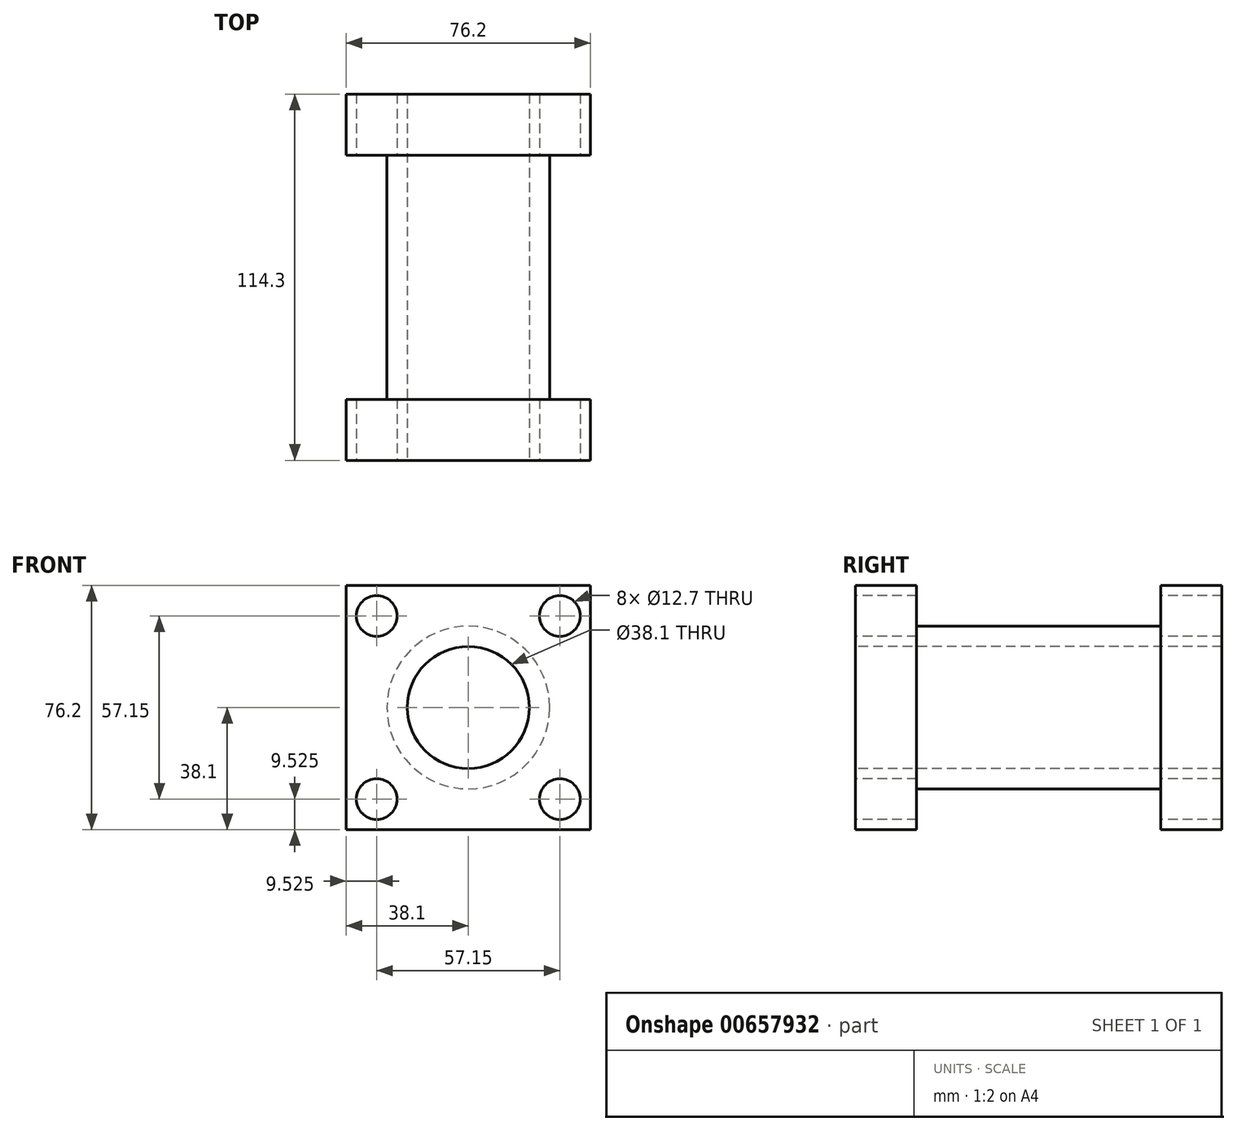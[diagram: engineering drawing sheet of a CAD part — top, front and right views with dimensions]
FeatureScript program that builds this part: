
annotation { "Feature Type Name" : "Feature", "Feature Type Description" : "" }
export const myFeature = defineFeature(function(context is Context, id is Id, definition is map)
    precondition{}
    {
        {
            var Q0;
            Q0=qCreatedBy(makeId("Front.planeOp"),FACE);
            var sketch = newSketch(context, id + "F0", { "sketchPlane" : qUnion([Q0])});
            skLineSegment(sketch, "E0.bottom", {"start": v(38.1, 38.1) * mm, "end": v(-38.1, 38.1) * mm});
            skLineSegment(sketch, "E0.top", {"start": v(38.1, -38.1) * mm, "end": v(-38.1, -38.1) * mm});
            skLineSegment(sketch, "E0.left", {"start": v(38.1, 38.1) * mm, "end": v(38.1, -38.1) * mm});
            skLineSegment(sketch, "E0.right", {"start": v(-38.1, 38.1) * mm, "end": v(-38.1, -38.1) * mm});
            skPoint(sketch, "E0.middle", {"position": v(0, 0) * mm});
            skSolve(sketch);
        }
        {
            var Q0;
            Q0=makeQuery(id+"F0.imprint","IMPRINT",FACE,{"disambiguationData":[TD([[makeQuery(id+"F0.imprint","IMPRINT",EDGE,{"derivedFrom":sQuery(id+"F0.wireOp",EDGE,"E0.bottom")}),1.0]])]});
            extrude(context, id + "F1", {"entities" : qUnion([Q0]), "depth" : 19.05 * mm, "offsetDistance" : 25.4 * mm});
        }
        {
            var Q0;
            Q0=makeQuery(id+"F1.opExtrude","CAP_FACE",FACE,{"disambiguationData":[OSD([sQuery(id+"F0.wireOp",EDGE,"E0.bottom"),sQuery(id+"F0.wireOp",EDGE,"E0.top"),sQuery(id+"F0.wireOp",EDGE,"E0.left"),sQuery(id+"F0.wireOp",EDGE,"E0.right")])],"isStart":false});
            var sketch = newSketch(context, id + "F2", { "sketchPlane" : qUnion([Q0])});
            skCircle(sketch, "E1", {"center": v(0, 0) * mm, "radius": 25.4 * mm});
            skSolve(sketch);
        }
        {
            var Q0;
            Q0=makeQuery(id+"F2.imprint","IMPRINT",FACE,{"disambiguationData":[TD([[makeQuery(id+"F2.imprint","IMPRINT",EDGE,{"derivedFrom":sQuery(id+"F2.wireOp",EDGE,"E1")}),1.0]])]});
            extrude(context, id + "F3", {"entities" : qUnion([Q0]), "operationType" : NewBodyOperationType.ADD, "depth" : 76.2 * mm, "offsetDistance" : 25.4 * mm});
        }
        {
            var Q0;
            Q0=makeQuery(id+"F3.opExtrude","CAP_FACE",FACE,{"disambiguationData":[OSD([sQuery(id+"F2.wireOp",EDGE,"E1")])],"isStart":false});
            var sketch = newSketch(context, id + "F4", { "sketchPlane" : qUnion([Q0])});
            skLineSegment(sketch, "E2.bottom", {"start": v(38.1, 38.1) * mm, "end": v(-38.1, 38.1) * mm});
            skLineSegment(sketch, "E2.top", {"start": v(38.1, -38.1) * mm, "end": v(-38.1, -38.1) * mm});
            skLineSegment(sketch, "E2.left", {"start": v(38.1, 38.1) * mm, "end": v(38.1, -38.1) * mm});
            skLineSegment(sketch, "E2.right", {"start": v(-38.1, 38.1) * mm, "end": v(-38.1, -38.1) * mm});
            skPoint(sketch, "E2.middle", {"position": v(0, 0) * mm});
            skSolve(sketch);
        }
        {
            var Q0;
            Q0=makeQuery(id+"F4.imprint","IMPRINT",FACE,{"disambiguationData":[TD([[makeQuery(id+"F4.imprint","IMPRINT",EDGE,{"derivedFrom":makeQuery(id+"F3.opExtrude","CAP_EDGE",EDGE,{"disambiguationData":[OSD([sQuery(id+"F2.wireOp",EDGE,"E1")])],"isStart":false})}),1.0]])]});
            var Q1;
            Q1=makeQuery(id+"F4.imprint","IMPRINT",FACE,{"disambiguationData":[TD([[makeQuery(id+"F4.imprint","IMPRINT",EDGE,{"derivedFrom":sQuery(id+"F4.wireOp",EDGE,"E2.bottom")}),1.0]])]});
            extrude(context, id + "F5", {"entities" : qUnion([Q0, Q1]), "operationType" : NewBodyOperationType.ADD, "depth" : 19.05 * mm, "offsetDistance" : 25.4 * mm});
        }
        {
            var Q0;
            Q0=makeQuery(id+"F5.opExtrude","CAP_FACE",FACE,{"disambiguationData":[OSD([sQuery(id+"F4.wireOp",EDGE,"E2.bottom"),sQuery(id+"F4.wireOp",EDGE,"E2.top"),sQuery(id+"F4.wireOp",EDGE,"E2.left"),sQuery(id+"F4.wireOp",EDGE,"E2.right")])],"isStart":false});
            var sketch = newSketch(context, id + "F6", { "sketchPlane" : qUnion([Q0])});
            skCircle(sketch, "E3", {"center": v(0, 0) * mm, "radius": 19.05 * mm});
            skSolve(sketch);
        }
        {
            var Q0;
            Q0=makeQuery(id+"F6.imprint","IMPRINT",FACE,{"disambiguationData":[TD([[makeQuery(id+"F6.imprint","IMPRINT",EDGE,{"derivedFrom":sQuery(id+"F6.wireOp",EDGE,"E3")}),1.0]])]});
            extrude(context, id + "F7", {"entities" : qUnion([Q0]), "operationType" : NewBodyOperationType.REMOVE, "oppositeDirection" : true, "depth" : 114.3 * mm, "offsetDistance" : 25.4 * mm});
        }
        {
            var Q0;
            Q0=makeQuery(id+"F5.opExtrude","CAP_FACE",FACE,{"disambiguationData":[OSD([sQuery(id+"F4.wireOp",EDGE,"E2.bottom"),sQuery(id+"F4.wireOp",EDGE,"E2.top"),sQuery(id+"F4.wireOp",EDGE,"E2.left"),sQuery(id+"F4.wireOp",EDGE,"E2.right")])],"isStart":false});
            var sketch = newSketch(context, id + "F8", { "sketchPlane" : qUnion([Q0])});
            skLineSegment(sketch, "E4", {"start": v(-38.1, 38.1) * mm, "end": v(-28.58, 38.1) * mm});
            skLineSegment(sketch, "E5", {"start": v(-28.58, 38.1) * mm, "end": v(-28.58, 28.58) * mm});
            skCircle(sketch, "E6", {"center": v(-28.58, 28.58) * mm, "radius": 6.35 * mm});
            skLineSegment(sketch, "E7", {"start": v(38.1, 38.1) * mm, "end": v(28.58, 38.1) * mm});
            skLineSegment(sketch, "E8", {"start": v(28.58, 38.1) * mm, "end": v(28.58, 28.58) * mm});
            skCircle(sketch, "E9", {"center": v(28.58, 28.58) * mm, "radius": 6.35 * mm});
            skLineSegment(sketch, "E10", {"start": v(-38.1, -38.1) * mm, "end": v(-28.58, -38.1) * mm});
            skLineSegment(sketch, "E11", {"start": v(-28.58, -38.1) * mm, "end": v(-28.58, -28.57) * mm});
            skCircle(sketch, "E12", {"center": v(-28.58, -28.57) * mm, "radius": 6.35 * mm});
            skLineSegment(sketch, "E13", {"start": v(38.1, -38.1) * mm, "end": v(28.58, -38.1) * mm});
            skLineSegment(sketch, "E14", {"start": v(28.58, -38.1) * mm, "end": v(28.58, -28.57) * mm});
            skCircle(sketch, "E15", {"center": v(28.58, -28.57) * mm, "radius": 6.35 * mm});
            skSolve(sketch);
        }
        {
            var Q0;
            Q0=makeQuery(id+"F8.imprint","IMPRINT",FACE,{"disambiguationData":[TD([[makeQuery(id+"F8.imprint","IMPRINT",EDGE,{"derivedFrom":sQuery(id+"F8.wireOp",EDGE,"E6")}),1.0]])]});
            var Q1;
            Q1=makeQuery(id+"F8.imprint","IMPRINT",FACE,{"disambiguationData":[TD([[makeQuery(id+"F8.imprint","IMPRINT",EDGE,{"derivedFrom":sQuery(id+"F8.wireOp",EDGE,"E12")}),1.0]])]});
            var Q2;
            Q2=makeQuery(id+"F8.imprint","IMPRINT",FACE,{"disambiguationData":[TD([[makeQuery(id+"F8.imprint","IMPRINT",EDGE,{"derivedFrom":sQuery(id+"F8.wireOp",EDGE,"E15")}),1.0]])]});
            var Q3;
            Q3=makeQuery(id+"F8.imprint","IMPRINT",FACE,{"disambiguationData":[TD([[makeQuery(id+"F8.imprint","IMPRINT",EDGE,{"derivedFrom":sQuery(id+"F8.wireOp",EDGE,"E9")}),1.0]])]});
            extrude(context, id + "F9", {"entities" : qUnion([Q0, Q1, Q2, Q3]), "operationType" : NewBodyOperationType.REMOVE, "oppositeDirection" : true, "depth" : 127 * mm, "offsetDistance" : 25.4 * mm});
        }
    });
